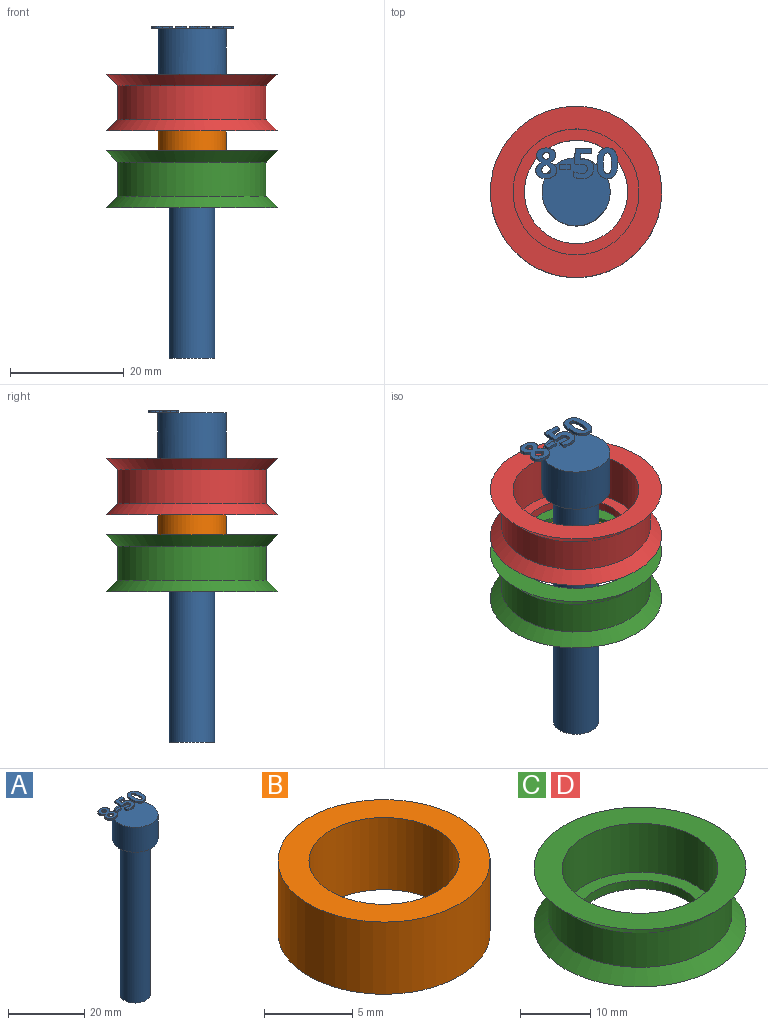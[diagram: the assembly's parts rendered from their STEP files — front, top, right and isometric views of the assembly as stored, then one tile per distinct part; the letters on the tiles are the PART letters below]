
ASSEMBLY  parts=4 mates=3
PART A: 86 faces, bbox 14.5x13.7x58.5 mm
  f0: plane 12x12mm, normal (0,0,1), area 99.4mm2, adj f5,f22,f23,f24,f25,f26,f40,f41
  f1: plane 1x0.26mm, normal (0,0,1), area 0.1mm2, adj f5,f46,f47,f48,f49
  f2: plane 0.85x0.68mm, normal (0,0,1), area 0.2mm2, adj f5,f29,f30,f31
  f3: cylinder r=4mm len=50mm, axis (0,0,-1), area 1256.6mm2, adj f4,f6
  f4: plane 8x8mm, normal (0,0,-1), area 50.3mm2, adj f3
  f5: cylinder r=6mm len=12mm, axis (0,0,-1), area 301.6mm2, adj f0,f1,f2,f6,f39,f45,f67,f85
  f6: plane 12x12mm, normal (0,0,-1), area 62.8mm2, adj f3,f5
  f7: extruded ~0.5x0.46mm, area 0.2mm2, adj f8,f37,f38,f39
  f8: extruded ~0.5x0.46mm, area 0.2mm2, adj f7,f9,f38,f39
  f9: extruded ~0.5x0.39mm, area 0.2mm2, adj f8,f10,f38,f39
  f10: extruded ~0.5x0.4mm, area 0.2mm2, adj f9,f11,f38,f39
  f11: extruded ~0.5x0.49mm, area 0.3mm2, adj f10,f12,f38,f39
  f12: extruded ~0.5x0.5mm, area 0.3mm2, adj f11,f13,f38,f39
  f13: extruded ~0.5x0.39mm, area 0.2mm2, adj f12,f37,f38,f39
  f14: extruded ~1.22x0.5mm, area 0.6mm2, adj f15,f35,f38,f39
  f15: extruded ~1.22x0.5mm, area 0.6mm2, adj f14,f16,f38,f39
  f16: extruded ~0.91x0.5mm, area 0.5mm2, adj f15,f17,f38,f39
  f17: extruded ~0.71x0.5mm, area 0.4mm2, adj f16,f18,f38,f39
  f18: extruded ~0.65x0.61mm, area 0.4mm2, adj f17,f19,f38,f39
  f19: extruded ~0.77x0.62mm, area 0.5mm2, adj f18,f20,f38,f39
  f20: extruded ~0.8x0.5mm, area 0.4mm2, adj f19,f21,f38,f39
  f21: extruded ~1.04x0.5mm, area 0.6mm2, adj f20,f22,f38,f39
  f22: extruded ~1.36x0.5mm, area 0.7mm2, adj f0,f21,f23,f38,f39
  f23: extruded ~1.33x0.5mm, area 0.7mm2, adj f0,f22,f24,f38
  f24: extruded ~1.04x0.51mm, area 0.6mm2, adj f0,f23,f25,f38
  f25: extruded ~0.75x0.5mm, area 0.4mm2, adj f0,f24,f26,f38
  f26: extruded ~0.85x0.66mm, area 0.5mm2, adj f0,f25,f27,f38,f39
  f27: extruded ~0.72x0.56mm, area 0.5mm2, adj f26,f28,f38,f39
  f28: extruded ~0.72x0.5mm, area 0.4mm2, adj f27,f35,f38,f39
  f29: extruded ~0.5x0.45mm, area 0.3mm2, adj f2,f30,f36,f38,f39
  f30: extruded ~0.5x0.47mm, area 0.3mm2, adj f2,f29,f31,f38
  f31: extruded ~0.62x0.5mm, area 0.3mm2, adj f2,f30,f32,f38,f39
  f32: extruded ~0.59x0.5mm, area 0.3mm2, adj f31,f33,f38,f39
  f33: extruded ~0.5x0.48mm, area 0.3mm2, adj f32,f34,f38,f39
  f34: extruded ~0.89x0.77mm, area 0.6mm2, adj f33,f36,f38,f39
  f35: extruded ~0.93x0.5mm, area 0.5mm2, adj f14,f28,f38,f39
  f36: extruded ~0.66x0.5mm, area 0.4mm2, adj f29,f34,f38,f39
  f37: extruded ~0.5x0.39mm, area 0.2mm2, adj f7,f13,f38,f39
  f38: plane 5.4x3.69mm, normal (0,0,1), area 12.7mm2, adj f7,f8,f9,f10,f11,f12,f13,f14
  f39: plane 5.4x3.53mm, normal (0,0,-1), area 10.2mm2, adj f5,f7,f8,f9,f10,f11,f12,f13
  f40: plane 0.9x0.5mm, normal (-1,0,0), area 0.4mm2, adj f0,f41,f43,f44
  f41: plane 1.93x0.5mm, normal (0,-1,0), area 1mm2, adj f0,f40,f42,f44
  f42: plane 0.9x0.5mm, normal (1,0,0), area 0.4mm2, adj f0,f41,f43,f44
  f43: plane 1.93x0.5mm, normal (0,1,0), area 1mm2, adj f0,f40,f42,f44
  f44: plane 1.93x0.9mm, normal (0,0,1), area 1.7mm2, adj f40,f41,f42,f43
  f45: plane 0.76x0.31mm, normal (0,0,-1), area 0mm2, adj f5,f46
  f46: extruded ~1.21x0.5mm, area 0.7mm2, adj f0,f1,f45,f47,f65,f66
  f47: extruded ~0.54x0.5mm, area 0.3mm2, adj f1,f46,f48,f66
  f48: plane 0.5x0.13mm, normal (-0.2,0.98,0), area 0.1mm2, adj f1,f47,f49,f66
  f49: plane 1.03x0.5mm, normal (1,-0.09,0), area 0.5mm2, adj f1,f48,f50,f66,f67
  f50: plane 1.88x0.5mm, normal (0,-1,0), area 0.9mm2, adj f49,f51,f66,f67
  f51: plane 0.94x0.5mm, normal (1,0,0), area 0.5mm2, adj f50,f52,f66,f67
  f52: plane 2.85x0.5mm, normal (0,1,0), area 1.4mm2, adj f51,f53,f66,f67
  f53: plane 2.68x0.5mm, normal (-1,0.07,0), area 1.3mm2, adj f0,f52,f54,f66,f67
  f54: plane 0.5x0.44mm, normal (-0.47,-0.88,0), area 0.3mm2, adj f0,f53,f55,f66
  f55: extruded ~0.5x0.37mm, area 0.2mm2, adj f0,f54,f56,f66
  f56: extruded ~0.5x0.42mm, area 0.2mm2, adj f0,f55,f57,f66
  f57: extruded ~1.05x0.8mm, area 0.8mm2, adj f0,f56,f58,f66
  f58: extruded ~1.02x0.83mm, area 0.8mm2, adj f0,f57,f59,f66
  f59: extruded ~0.72x0.5mm, area 0.4mm2, adj f0,f58,f60,f66
  f60: extruded ~0.66x0.5mm, area 0.4mm2, adj f0,f59,f61,f66
  f61: plane 0.96x0.5mm, normal (-1,0,0), area 0.5mm2, adj f0,f60,f62,f66
  f62: extruded ~1.42x0.5mm, area 0.7mm2, adj f0,f61,f63,f66
  f63: extruded ~1.55x0.5mm, area 0.8mm2, adj f0,f62,f64,f66
  f64: extruded ~1.36x0.54mm, area 0.8mm2, adj f0,f63,f65,f66
  f65: extruded ~1.17x0.5mm, area 0.6mm2, adj f0,f46,f64,f66
  f66: plane 5.33x3.51mm, normal (0,0,1), area 10.9mm2, adj f46,f47,f48,f49,f50,f51,f52,f53
  f67: plane 2.97x1.71mm, normal (0,0,-1), area 3.5mm2, adj f5,f49,f50,f51,f52,f53
  f68: extruded ~1.39x0.5mm, area 0.7mm2, adj f69,f83,f84,f85
  f69: extruded ~1.39x0.5mm, area 0.7mm2, adj f68,f70,f84,f85
  f70: extruded ~0.56x0.5mm, area 0.4mm2, adj f69,f71,f84,f85
  f71: extruded ~0.56x0.5mm, area 0.4mm2, adj f70,f72,f84,f85
  f72: extruded ~1.39x0.5mm, area 0.7mm2, adj f71,f73,f84,f85
  f73: extruded ~1.38x0.5mm, area 0.7mm2, adj f72,f74,f84,f85
  f74: extruded ~0.56x0.5mm, area 0.4mm2, adj f73,f83,f84,f85
  f75: extruded ~2.04x0.5mm, area 1.1mm2, adj f76,f82,f84,f85
  f76: extruded ~2.02x0.5mm, area 1.1mm2, adj f75,f77,f84,f85
  f77: extruded ~1.38x0.69mm, area 0.8mm2, adj f76,f78,f84,f85
  f78: extruded ~1.38x0.66mm, area 0.8mm2, adj f77,f79,f84,f85
  f79: extruded ~2.05x0.5mm, area 1.1mm2, adj f78,f80,f84,f85
  f80: extruded ~2.02x0.5mm, area 1mm2, adj f0,f79,f81,f84,f85
  f81: extruded ~1.37x0.68mm, area 0.8mm2, adj f0,f80,f82,f84
  f82: extruded ~1.39x0.66mm, area 0.8mm2, adj f0,f75,f81,f84,f85
  f83: extruded ~0.56x0.5mm, area 0.4mm2, adj f68,f74,f84,f85
  f84: plane 5.41x3.68mm, normal (0,0,1), area 12.1mm2, adj f68,f69,f70,f71,f72,f73,f74,f75
  f85: plane 5.41x3.68mm, normal (0,0,-1), area 10.3mm2, adj f5,f68,f69,f70,f71,f72,f73,f74
PART B: 4 faces, bbox 12x12x5 mm
  f0: cylinder r=4.25mm len=8.5mm, axis (0,0,-1), area 133.5mm2, adj f2,f3
  f1: cylinder r=6mm len=12mm, axis (0,0,-1), area 188.5mm2, adj f2,f3
  f2: plane 12x12mm, normal (0,0,1), area 56.4mm2, adj f0,f1
  f3: plane 12x12mm, normal (0,0,-1), area 56.4mm2, adj f0,f1
PART C: 8 faces, bbox 30.2x30.2x10 mm
  f0: plane 30.2x30.2mm, normal (0,0,1), area 329.2mm2, adj f1,f7
  f1: cylinder r=11.1mm len=22.2mm, axis (0,0,-1), area 592.8mm2, adj f0,f2
  f2: plane 22.2x22.2mm, normal (0,0,1), area 126.9mm2, adj f1,f3
  f3: cylinder r=9.1mm len=18.2mm, axis (0,0,-1), area 85.8mm2, adj f2,f4
  f4: plane 30.2x30.2mm, normal (0,0,-1), area 456.2mm2, adj f3,f5
  f5: cone r=13.1mm half-angle=45deg, axis (0,0,-1), area 250.6mm2, adj f4,f6
  f6: cylinder r=13.1mm len=26.2mm, axis (0,0,-1), area 493.9mm2, adj f5,f7
  f7: cone r=15.1mm half-angle=45deg, axis (0,0,1), area 250.6mm2, adj f0,f6
PART D: same geometry as C
PLACE A t=(-103.78,-12.5,-13.6)mm
PLACE B rot(axis=(1,0,0),180deg) t=(-103.78,-12.5,26.4)mm
PLACE C t=(-103.78,-12.5,18.1)mm
PLACE D t=(-103.78,-12.5,31.6)mm
MATE fastened A.f3 <-> D.f1  axis (0,0,-1) through (-103.78,-12.5,36.4)mm
MATE fastened B.f0 <-> C.f1  axis (0,0,1) through (-103.78,-12.5,21.4)mm
MATE fastened D.f1 <-> B.f0  axis (0,0,-1) through (-103.78,-12.5,26.4)mm
